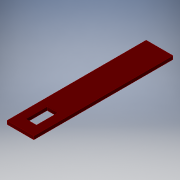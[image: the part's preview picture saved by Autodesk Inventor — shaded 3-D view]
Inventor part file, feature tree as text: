
AUTODESK INVENTOR PART (.ipt)
format: ipt  version: 2019 (Build 230136000, 136)  size: 123,392 bytes
history: native  units: mm
features: extrude x1, sketch x1
ambient origin geometry x8: Origin, YZ Plane, XZ Plane, XY Plane, X Axis, Y Axis, Z Axis, Center Point
bodies: Body1 (feature_tree)
feature tree (2):
  extrude  "Extrusion2"  Depth=10.0mm
  sketch  "Sketch1"  dims[d16=15.0mm d18=3.18mm d19=15.0mm d20=7.5mm d21=1.59mm d24=10.0mm d25=20.0mm d26=25.0mm d27=130.0mm d28=20.0mm d29=12.5mm d30=12.5mm d31=12.5mm d32=3.18mm d35=3.18mm d36=0.0mm]
